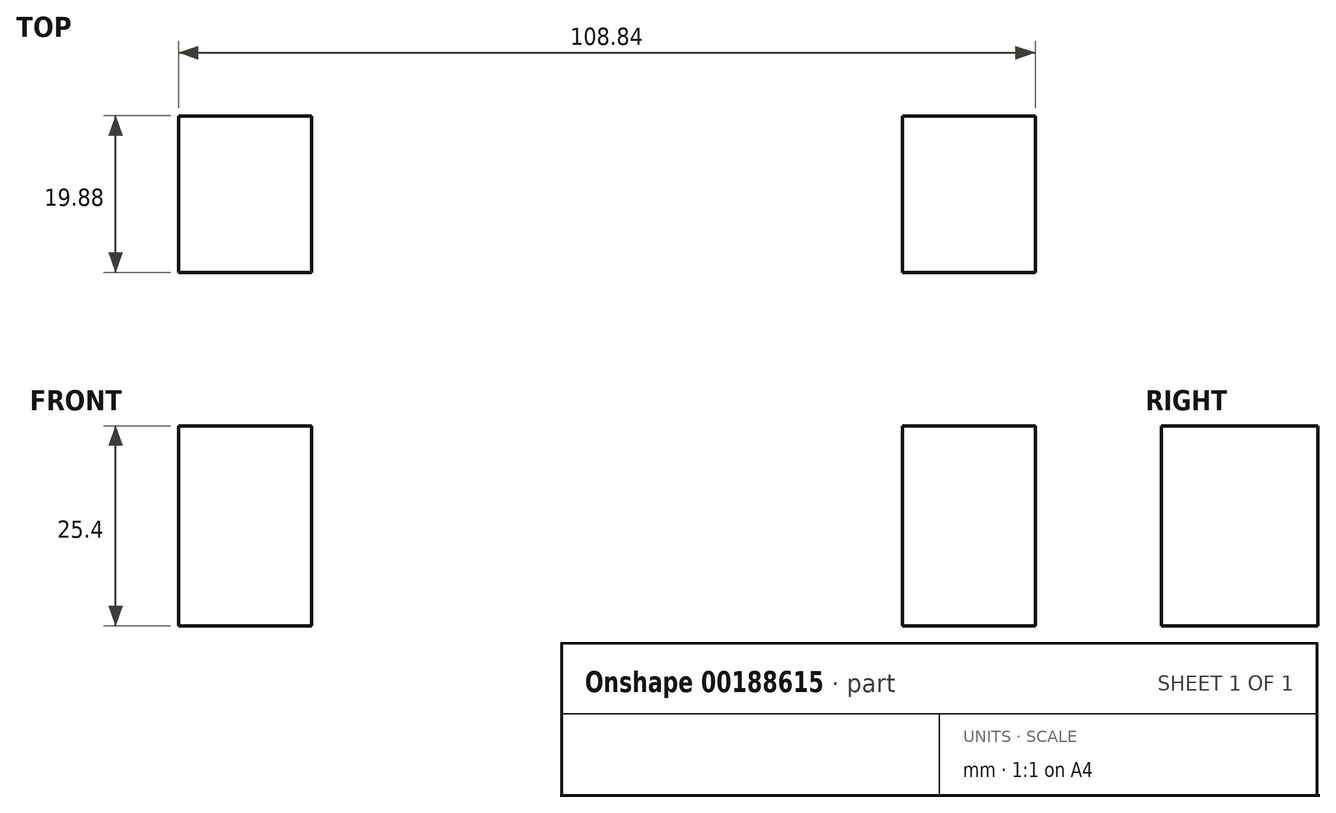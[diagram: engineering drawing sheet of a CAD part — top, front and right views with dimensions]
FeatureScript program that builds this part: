
annotation { "Feature Type Name" : "Feature", "Feature Type Description" : "" }
export const myFeature = defineFeature(function(context is Context, id is Id, definition is map)
    precondition{}
    {
        {
            var Q0;
            Q0=qCreatedBy(makeId("Top.planeOp"),FACE);
            var sketch = newSketch(context, id + "F0", { "sketchPlane" : qUnion([Q0])});
            skLineSegment(sketch, "E0.bottom", {"start": v(-54.42, 34.79) * mm, "end": v(-37.52, 34.79) * mm});
            skLineSegment(sketch, "E0.top", {"start": v(-54.42, 14.9) * mm, "end": v(-37.52, 14.9) * mm});
            skLineSegment(sketch, "E0.left", {"start": v(-54.42, 34.79) * mm, "end": v(-54.42, 14.9) * mm});
            skLineSegment(sketch, "E0.right", {"start": v(-37.52, 34.79) * mm, "end": v(-37.52, 14.9) * mm});
            skSolve(sketch);
        }
        {
            var Q0;
            Q0=makeQuery(id+"F0.imprint","IMPRINT",FACE,{"disambiguationData":[TD([[makeQuery(id+"F0.imprint","IMPRINT",EDGE,{"derivedFrom":sQuery(id+"F0.wireOp",EDGE,"E0.bottom")}),-1.0]])]});
            extrude(context, id + "F1", {"entities" : qUnion([Q0]), "depth" : 25.4 * mm});
        }
        {
            var Q0;
            Q0=makeQuery(id+"F1.opExtrude","SWEPT_BODY",BODY,{"disambiguationData":[OSD([sQuery(id+"F0.wireOp",EDGE,"E0.bottom"),sQuery(id+"F0.wireOp",EDGE,"E0.top"),sQuery(id+"F0.wireOp",EDGE,"E0.left"),sQuery(id+"F0.wireOp",EDGE,"E0.right")])]});
            var Q1;
            Q1=makeQuery(id+"F1.opExtrude","SWEPT_FACE",FACE,{"disambiguationData":[OSD([sQuery(id+"F0.wireOp",EDGE,"E0.right")])]});
            var Q2;
            Q2=makeQuery(id+"F1.opExtrude","SWEPT_FACE",FACE,{"disambiguationData":[OSD([sQuery(id+"F0.wireOp",EDGE,"E0.top")])]});
            var Q3;
            Q3=makeQuery(id+"F1.opExtrude","CAP_FACE",FACE,{"disambiguationData":[OSD([sQuery(id+"F0.wireOp",EDGE,"E0.bottom"),sQuery(id+"F0.wireOp",EDGE,"E0.top"),sQuery(id+"F0.wireOp",EDGE,"E0.left"),sQuery(id+"F0.wireOp",EDGE,"E0.right")])],"isStart":false});
            var Q4;
            Q4=makeQuery(id+"F1.opExtrude","SWEPT_FACE",FACE,{"disambiguationData":[OSD([sQuery(id+"F0.wireOp",EDGE,"E0.left")])]});
            var Q5;
            Q5=makeQuery(id+"F1.opExtrude","SWEPT_FACE",FACE,{"disambiguationData":[OSD([sQuery(id+"F0.wireOp",EDGE,"E0.bottom")])]});
            var Q6;
            Q6=makeQuery(id+"F1.opExtrude","CAP_FACE",FACE,{"disambiguationData":[OSD([sQuery(id+"F0.wireOp",EDGE,"E0.bottom"),sQuery(id+"F0.wireOp",EDGE,"E0.top"),sQuery(id+"F0.wireOp",EDGE,"E0.left"),sQuery(id+"F0.wireOp",EDGE,"E0.right")])],"isStart":true});
            var Q7;
            Q7=qCreatedBy(makeId("Right.planeOp"),FACE);
            mirror(context, id + "F2", {"patternType" : MirrorType.FACE, "entities" : qUnion([Q0]), "faces" : qUnion([Q1, Q2, Q3, Q4, Q5, Q6]), "mirrorPlane" : qUnion([Q7])});
        }
    });
